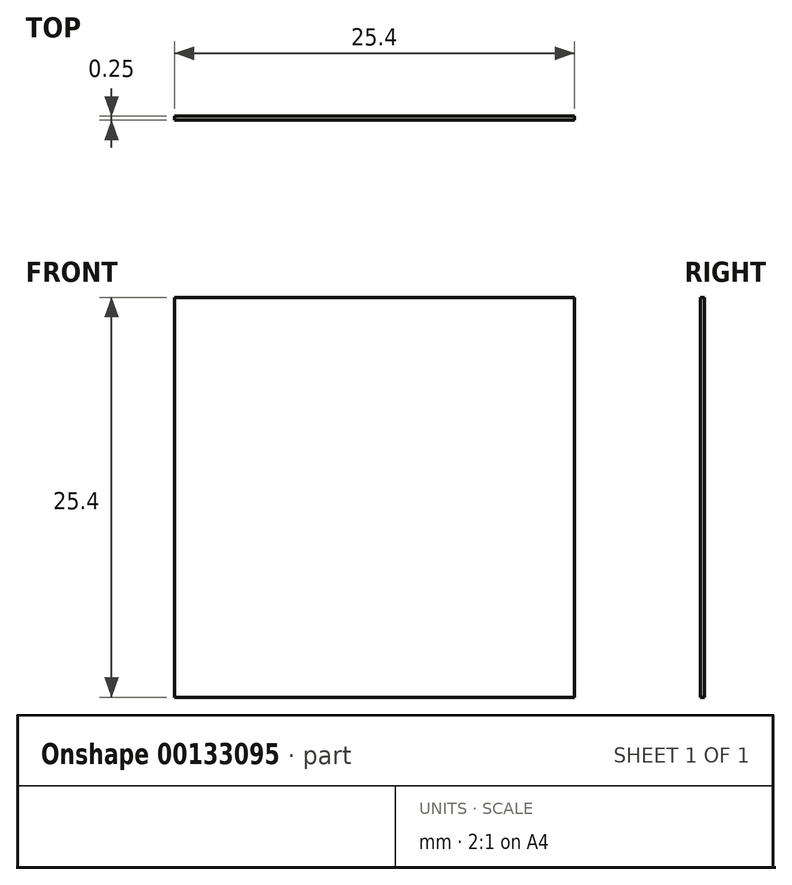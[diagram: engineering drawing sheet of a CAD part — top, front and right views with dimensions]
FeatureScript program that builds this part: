
annotation { "Feature Type Name" : "Feature", "Feature Type Description" : "" }
export const myFeature = defineFeature(function(context is Context, id is Id, definition is map)
    precondition{}
    {
        {
            var Q0;
            Q0=qCreatedBy(makeId("Front.planeOp"),FACE);
            var sketch = newSketch(context, id + "F0", { "sketchPlane" : qUnion([Q0])});
            skLineSegment(sketch, "E0.bottom", {"start": v(-12.7, 12.7) * mm, "end": v(12.7, 12.7) * mm});
            skLineSegment(sketch, "E0.top", {"start": v(-12.7, -12.7) * mm, "end": v(12.7, -12.7) * mm});
            skLineSegment(sketch, "E0.left", {"start": v(-12.7, 12.7) * mm, "end": v(-12.7, -12.7) * mm});
            skLineSegment(sketch, "E0.right", {"start": v(12.7, 12.7) * mm, "end": v(12.7, -12.7) * mm});
            skPoint(sketch, "E0.middle", {"position": v(0, 0) * mm});
            skSolve(sketch);
        }
        {
            var Q0;
            Q0 = qSketchRegion(id + "F0", true);
            extrude(context, id + "F1", {"entities" : qUnion([Q0]), "depth" : 0.25 * mm});
        }
    });
